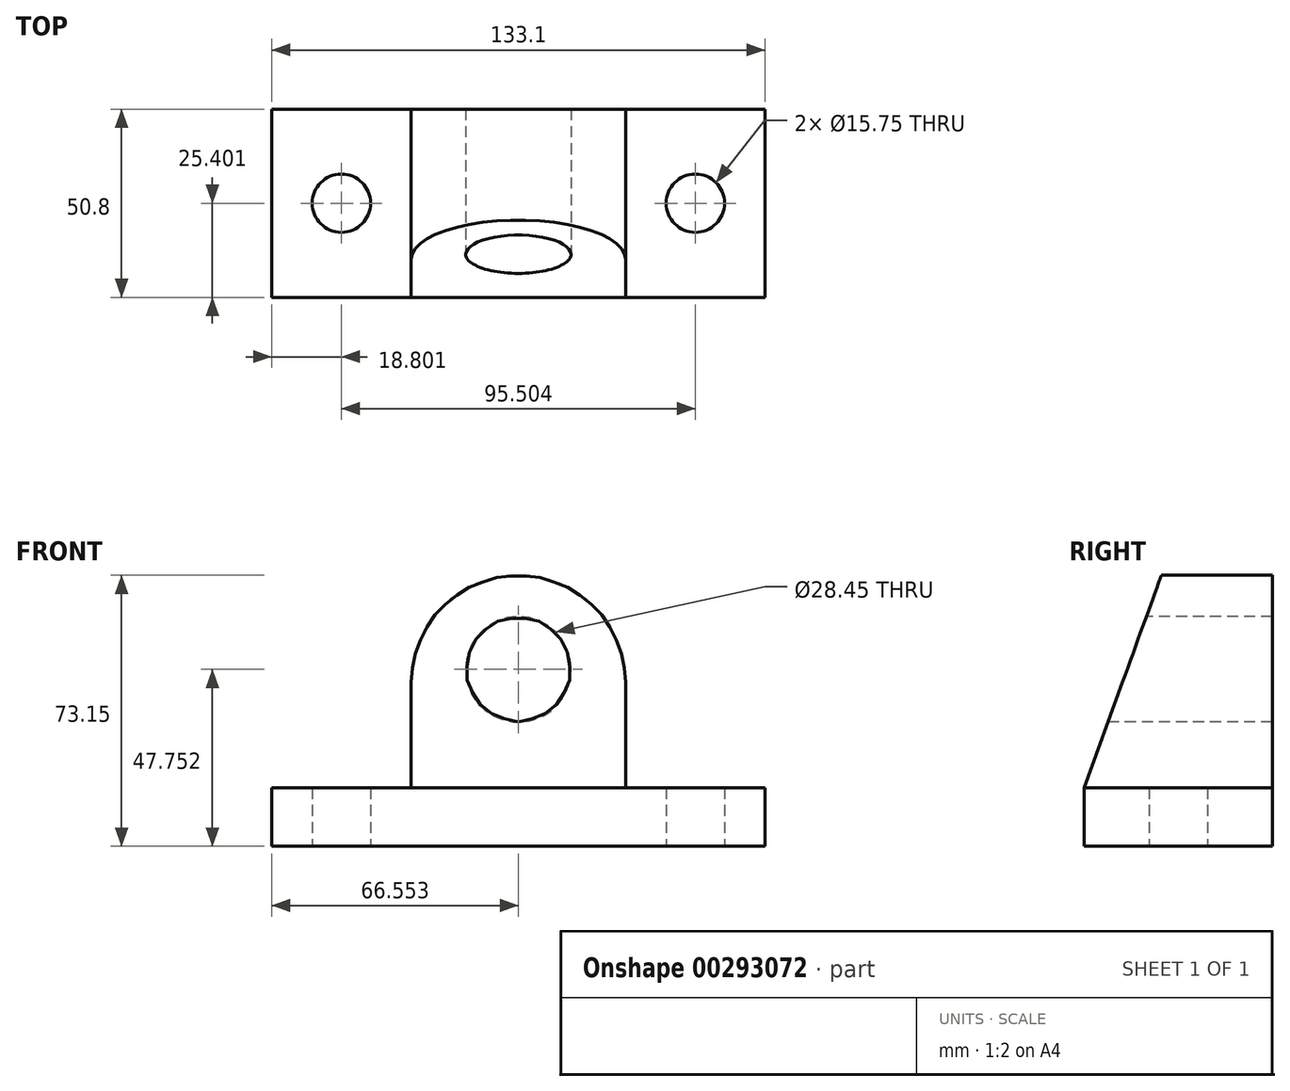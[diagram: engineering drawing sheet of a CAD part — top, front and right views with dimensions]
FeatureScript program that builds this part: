
annotation { "Feature Type Name" : "Feature", "Feature Type Description" : "" }
export const myFeature = defineFeature(function(context is Context, id is Id, definition is map)
    precondition{}
    {
        {
            var Q0;
            Q0=qCreatedBy(makeId("Top.planeOp"),FACE);
            var sketch = newSketch(context, id + "F0", { "sketchPlane" : qUnion([Q0])});
            skLineSegment(sketch, "E0.bottom", {"start": v(-53.35, 3.15) * mm, "end": v(79.75, 3.15) * mm});
            skLineSegment(sketch, "E0.top", {"start": v(-53.35, -47.65) * mm, "end": v(79.75, -47.65) * mm});
            skLineSegment(sketch, "E0.left", {"start": v(-53.35, 3.15) * mm, "end": v(-53.35, -47.65) * mm});
            skLineSegment(sketch, "E0.right", {"start": v(79.75, 3.15) * mm, "end": v(79.75, -47.65) * mm});
            skLineSegment(sketch, "E1", {"start": v(-8.52, -40.67) * mm, "end": v(-8.52, -40.67) * mm});
            skLineSegment(sketch, "E2", {"start": v(79.75, -47.65) * mm, "end": v(13.2, -47.65) * mm});
            skLineSegment(sketch, "E3", {"start": v(13.2, -47.65) * mm, "end": v(13.2, 3.15) * mm});
            skLineSegment(sketch, "E4", {"start": v(13.2, -22.25) * mm, "end": v(60.95, -22.25) * mm});
            skCircle(sketch, "E5", {"center": v(60.95, -22.25) * mm, "radius": 7.87 * mm});
            skCircle(sketch, "E6.MirrorC", {"center": v(-34.55, -22.25) * mm, "radius": 7.87 * mm});
            skSolve(sketch);
        }
        {
            var Q0;
            Q0 = qSketchRegion(id + "F0", true);
            extrude(context, id + "F1", {"entities" : qUnion([Q0]), "depth" : 15.75 * mm});
        }
        {
            var Q0;
            Q0=makeQuery(id+"F1.opExtrude","CAP_FACE",FACE,{"disambiguationData":[OSD([sQuery(id+"F0.wireOp",EDGE,"E0.bottom"),sQuery(id+"F0.wireOp",EDGE,"E0.top"),sQuery(id+"F0.wireOp",EDGE,"E0.left"),sQuery(id+"F0.wireOp",EDGE,"E0.right"),sQuery(id+"F0.wireOp",EDGE,"E2"),sQuery(id+"F0.wireOp",EDGE,"E5"),sQuery(id+"F0.wireOp",EDGE,"E6.MirrorC")])],"isStart":false});
            var sketch = newSketch(context, id + "F2", { "sketchPlane" : qUnion([Q0])});
            skLineSegment(sketch, "E7", {"start": v(-53.35, -47.65) * mm, "end": v(-15.75, -47.65) * mm});
            skLineSegment(sketch, "E8", {"start": v(79.75, -47.65) * mm, "end": v(42.16, -47.65) * mm});
            skLineSegment(sketch, "E9.bottom", {"start": v(-15.75, -47.65) * mm, "end": v(42.16, -47.65) * mm});
            skLineSegment(sketch, "E9.top", {"start": v(-15.75, 3.15) * mm, "end": v(42.16, 3.15) * mm});
            skLineSegment(sketch, "E9.left", {"start": v(-15.75, -47.65) * mm, "end": v(-15.75, 3.15) * mm});
            skLineSegment(sketch, "E9.right", {"start": v(42.16, -47.65) * mm, "end": v(42.16, 3.15) * mm});
            skSolve(sketch);
        }
        {
            var Q0;
            Q0=makeQuery(id+"F2.imprint","IMPRINT",FACE,{"disambiguationData":[TD([[makeQuery(id+"F2.imprint","IMPRINT",EDGE,{"derivedFrom":sQuery(id+"F2.wireOp",EDGE,"E9.bottom")}),1.0]])]});
            extrude(context, id + "F3", {"entities" : qUnion([Q0]), "operationType" : NewBodyOperationType.ADD, "depth" : 3.05 * mm});
        }
        {
            var Q0;
            Q0=makeQuery(id+"F3.opExtrude","CAP_FACE",FACE,{"disambiguationData":[OSD([sQuery(id+"F2.wireOp",EDGE,"E9.bottom"),sQuery(id+"F2.wireOp",EDGE,"E9.top"),sQuery(id+"F2.wireOp",EDGE,"E9.left"),sQuery(id+"F2.wireOp",EDGE,"E9.right")])],"isStart":false});
            extrude(context, id + "F4", {"entities" : qUnion([Q0]), "operationType" : NewBodyOperationType.ADD, "depth" : 25.4 * mm});
        }
        {
            var Q0;
            {var subQ0=sQuery(id+"F2.wireOp",EDGE,"E9.bottom");Q0=makeQuery(id+"F4.boolean.opBoolean","MERGE",FACE,{"derivedFrom":[makeQuery(id+"F3.boolean.opBoolean","MERGE",FACE,{"derivedFrom":[makeQuery(id+"F1.opExtrude","SWEPT_FACE",FACE,{"disambiguationData":[OSD([sQuery(id+"F0.wireOp",EDGE,"E0.top"),sQuery(id+"F0.wireOp",EDGE,"E2")])]}),makeQuery(id+"F3.opExtrude","SWEPT_FACE",FACE,{"disambiguationData":[OSD([subQ0])]})]}),makeQuery(id+"F4.opExtrude","SWEPT_FACE",FACE,{"disambiguationData":[OSD([subQ0])]})]});}
            var sketch = newSketch(context, id + "F5", { "sketchPlane" : qUnion([Q0])});
            skCircle(sketch, "E10", {"center": v(13.2, 44.2) * mm, "radius": 28.96 * mm});
            skSolve(sketch);
        }
        {
            var Q0;
            Q0 = qSketchRegion(id + "F5", true);
            extrude(context, id + "F6", {"entities" : qUnion([Q0]), "operationType" : NewBodyOperationType.ADD, "oppositeDirection" : true, "depth" : 50.8 * mm});
        }
        {
            var Q0;
            {var subQ0=sQuery(id+"F2.wireOp",EDGE,"E9.bottom");Q0=makeQuery(id+"F6.boolean.opBoolean","MERGE",FACE,{"derivedFrom":[makeQuery(id+"F4.boolean.opBoolean","MERGE",FACE,{"derivedFrom":[makeQuery(id+"F3.boolean.opBoolean","MERGE",FACE,{"derivedFrom":[makeQuery(id+"F1.opExtrude","SWEPT_FACE",FACE,{"disambiguationData":[OSD([sQuery(id+"F0.wireOp",EDGE,"E0.top"),sQuery(id+"F0.wireOp",EDGE,"E2")])]}),makeQuery(id+"F3.opExtrude","SWEPT_FACE",FACE,{"disambiguationData":[OSD([subQ0])]})]}),makeQuery(id+"F4.opExtrude","SWEPT_FACE",FACE,{"disambiguationData":[OSD([subQ0])]})]}),makeQuery(id+"F6.opExtrude","CAP_FACE",FACE,{"disambiguationData":[OSD([sQuery(id+"F5.wireOp",EDGE,"E10")])],"isStart":true})]});}
            var sketch = newSketch(context, id + "F7", { "sketchPlane" : qUnion([Q0])});
            skLineSegment(sketch, "E11", {"start": v(13.2, 73.15) * mm, "end": v(13.2, 47.75) * mm});
            skCircle(sketch, "E12", {"center": v(13.2, 47.75) * mm, "radius": 14.22 * mm});
            skSolve(sketch);
        }
        {
            var Q0;
            Q0 = qSketchRegion(id + "F7", true);
            extrude(context, id + "F8", {"entities" : qUnion([Q0]), "operationType" : NewBodyOperationType.REMOVE, "oppositeDirection" : true, "depth" : 50.8 * mm});
        }
        {
            var Q0;
            {var subQ0=sQuery(id+"F2.wireOp",EDGE,"E9.right");Q0=makeQuery(id+"F4.boolean.opBoolean","MERGE",FACE,{"derivedFrom":[makeQuery(id+"F3.opExtrude","SWEPT_FACE",FACE,{"disambiguationData":[OSD([subQ0])]}),makeQuery(id+"F4.opExtrude","SWEPT_FACE",FACE,{"disambiguationData":[OSD([subQ0])]})]});}
            var sketch = newSketch(context, id + "F9", { "sketchPlane" : qUnion([Q0])});
            skLineSegment(sketch, "E13", {"start": v(-47.65, 15.75) * mm, "end": v(-26.6, 73.57) * mm});
            skLineSegment(sketch, "E14", {"start": v(-26.6, 73.57) * mm, "end": v(-47.65, 73.57) * mm});
            skLineSegment(sketch, "E15", {"start": v(-47.65, 73.57) * mm, "end": v(-47.65, 15.75) * mm});
            skSolve(sketch);
        }
        {
            var Q0;
            Q0 = qSketchRegion(id + "F9", true);
            extrude(context, id + "F10", {"entities" : qUnion([Q0]), "operationType" : NewBodyOperationType.REMOVE, "oppositeDirection" : true, "depth" : 177.8 * mm});
        }
    });
